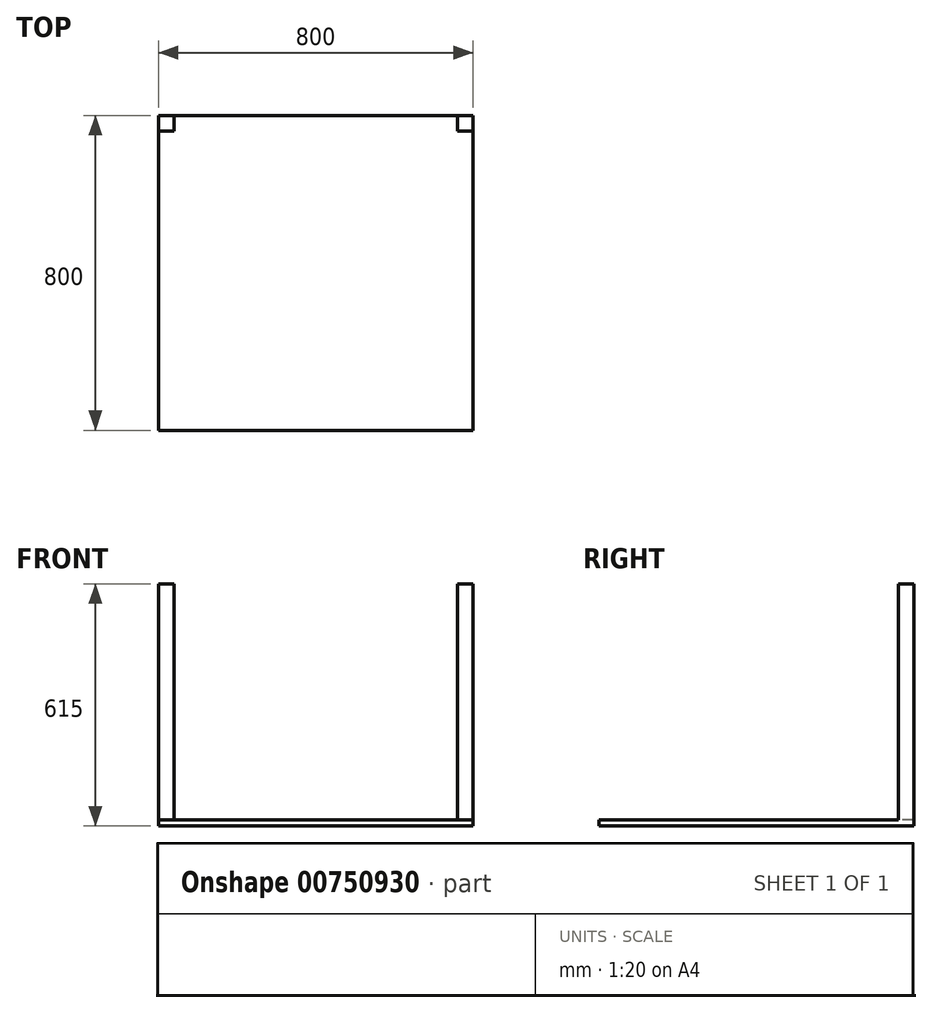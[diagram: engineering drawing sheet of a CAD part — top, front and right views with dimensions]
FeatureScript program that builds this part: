
annotation { "Feature Type Name" : "Feature", "Feature Type Description" : "" }
export const myFeature = defineFeature(function(context is Context, id is Id, definition is map)
    precondition{}
    {
        {
            var Q0;
            Q0=qCreatedBy(makeId("Top.planeOp"),FACE);
            var sketch = newSketch(context, id + "F0", { "sketchPlane" : qUnion([Q0])});
            skLineSegment(sketch, "E0.bottom", {"start": v(400, -400) * mm, "end": v(-400, -400) * mm});
            skLineSegment(sketch, "E0.top", {"start": v(400, 400) * mm, "end": v(-400, 400) * mm});
            skLineSegment(sketch, "E0.left", {"start": v(400, -400) * mm, "end": v(400, 400) * mm});
            skLineSegment(sketch, "E0.right", {"start": v(-400, -400) * mm, "end": v(-400, 400) * mm});
            skPoint(sketch, "E0.middle", {"position": v(0, 0) * mm});
            skSolve(sketch);
        }
        {
            var Q0;
            Q0 = qSketchRegion(id + "F0", true);
            extrude(context, id + "F1", {"entities" : qUnion([Q0]), "depth" : 15 * mm, "offsetDistance" : 25 * mm});
        }
        {
            var Q0;
            Q0=makeQuery(id+"F1.opExtrude","CAP_FACE",FACE,{"disambiguationData":[OSD([sQuery(id+"F0.wireOp",EDGE,"E0.bottom"),sQuery(id+"F0.wireOp",EDGE,"E0.top"),sQuery(id+"F0.wireOp",EDGE,"E0.left"),sQuery(id+"F0.wireOp",EDGE,"E0.right")])],"isStart":false});
            var sketch = newSketch(context, id + "F2", { "sketchPlane" : qUnion([Q0])});
            skLineSegment(sketch, "E1.bottom", {"start": v(400, 400) * mm, "end": v(360, 400) * mm});
            skLineSegment(sketch, "E1.top", {"start": v(400, 360) * mm, "end": v(360, 360) * mm});
            skLineSegment(sketch, "E1.left", {"start": v(400, 400) * mm, "end": v(400, 360) * mm});
            skLineSegment(sketch, "E1.right", {"start": v(360, 400) * mm, "end": v(360, 360) * mm});
            skLineSegment(sketch, "E2.bottom", {"start": v(-400, 400) * mm, "end": v(-360, 400) * mm});
            skLineSegment(sketch, "E2.top", {"start": v(-400, 360) * mm, "end": v(-360, 360) * mm});
            skLineSegment(sketch, "E2.left", {"start": v(-400, 400) * mm, "end": v(-400, 360) * mm});
            skLineSegment(sketch, "E2.right", {"start": v(-360, 400) * mm, "end": v(-360, 360) * mm});
            skSolve(sketch);
        }
        {
            var Q0;
            Q0 = qSketchRegion(id + "F2", true);
            extrude(context, id + "F3", {"entities" : qUnion([Q0]), "operationType" : NewBodyOperationType.ADD, "depth" : 600 * mm, "offsetDistance" : 25 * mm});
        }
    });
